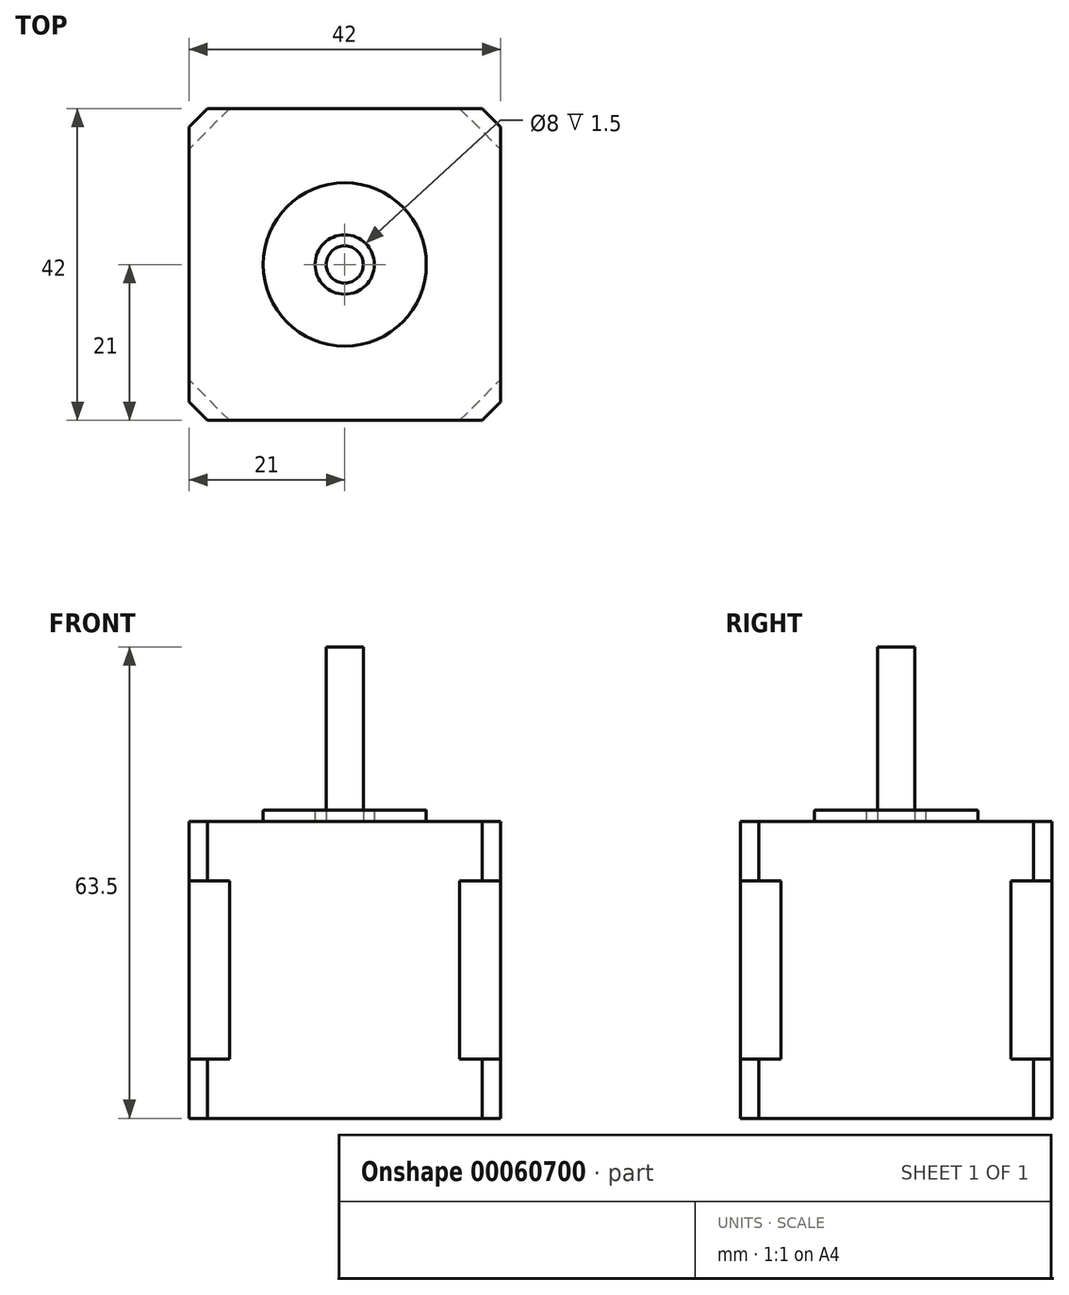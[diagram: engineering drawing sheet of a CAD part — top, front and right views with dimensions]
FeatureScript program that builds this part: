
annotation { "Feature Type Name" : "Feature", "Feature Type Description" : "" }
export const myFeature = defineFeature(function(context is Context, id is Id, definition is map)
    precondition{}
    {
        {
            var Q0;
            Q0=qCreatedBy(makeId("Top.planeOp"),FACE);
            var sketch = newSketch(context, id + "F0", { "sketchPlane" : qUnion([Q0])});
            skLineSegment(sketch, "E0.rect.bottom", {"start": v(21, 21) * mm, "end": v(-21, 21) * mm});
            skLineSegment(sketch, "E0.rect.top", {"start": v(21, -21) * mm, "end": v(-21, -21) * mm});
            skLineSegment(sketch, "E0.rect.left", {"start": v(21, 21) * mm, "end": v(21, -21) * mm});
            skLineSegment(sketch, "E0.rect.right", {"start": v(-21, 21) * mm, "end": v(-21, -21) * mm});
            skPoint(sketch, "E0.rect.middle", {"position": v(0, 0) * mm});
            skSolve(sketch);
        }
        {
            var Q0;
            Q0=makeQuery(id+"F0.imprint","IMPRINT",FACE,{"disambiguationData":[TD([[makeQuery(id+"F0.imprint","IMPRINT",EDGE,{"derivedFrom":sQuery(id+"F0.wireOp",EDGE,"E0.rect.bottom")}),1.0]])]});
            var Q1;
            Q1 = qSketchRegion(id + "FU1vRKXK89ZEF6C_1", true);
            extrude(context, id + "F1", {"entities" : qUnion([Q0, Q1]), "depth" : 8 * mm});
        }
        {
            var Q0;
            Q0=makeQuery(id+"F1.opExtrude","CAP_FACE",FACE,{"disambiguationData":[OSD([sQuery(id+"F0.wireOp",EDGE,"E0.rect.bottom"),sQuery(id+"F0.wireOp",EDGE,"E0.rect.top"),sQuery(id+"F0.wireOp",EDGE,"E0.rect.left"),sQuery(id+"F0.wireOp",EDGE,"E0.rect.right")])],"isStart":false});
            extrude(context, id + "F2", {"entities" : qUnion([Q0]), "depth" : 24 * mm});
        }
        {
            var Q0;
            Q0=makeQuery(id+"F2.opExtrude","CAP_FACE",FACE,{"disambiguationData":[OSD([sQuery(id+"F0.wireOp",EDGE,"E0.rect.bottom"),sQuery(id+"F0.wireOp",EDGE,"E0.rect.top"),sQuery(id+"F0.wireOp",EDGE,"E0.rect.left"),sQuery(id+"F0.wireOp",EDGE,"E0.rect.right")])],"isStart":false});
            extrude(context, id + "F3", {"entities" : qUnion([Q0]), "depth" : 8 * mm});
        }
        {
            var Q0;
            Q0=makeQuery(id+"F1.opExtrude","SWEPT_EDGE",EDGE,{"disambiguationData":[OSD([sQuery(id+"F0.wireOp",EDGE,"E0.rect.top"),sQuery(id+"F0.wireOp",EDGE,"E0.rect.right")])]});
            var Q1;
            Q1=makeQuery(id+"F3.opExtrude","SWEPT_EDGE",EDGE,{"disambiguationData":[OSD([sQuery(id+"F0.wireOp",EDGE,"E0.rect.top"),sQuery(id+"F0.wireOp",EDGE,"E0.rect.right")])]});
            var Q2;
            Q2=makeQuery(id+"F3.opExtrude","SWEPT_EDGE",EDGE,{"disambiguationData":[OSD([sQuery(id+"F0.wireOp",EDGE,"E0.rect.bottom"),sQuery(id+"F0.wireOp",EDGE,"E0.rect.right")])]});
            var Q3;
            Q3=makeQuery(id+"F1.opExtrude","SWEPT_EDGE",EDGE,{"disambiguationData":[OSD([sQuery(id+"F0.wireOp",EDGE,"E0.rect.bottom"),sQuery(id+"F0.wireOp",EDGE,"E0.rect.right")])]});
            var Q4;
            Q4=makeQuery(id+"F3.opExtrude","SWEPT_EDGE",EDGE,{"disambiguationData":[OSD([sQuery(id+"F0.wireOp",EDGE,"E0.rect.bottom"),sQuery(id+"F0.wireOp",EDGE,"E0.rect.left")])]});
            var Q5;
            Q5=makeQuery(id+"F1.opExtrude","SWEPT_EDGE",EDGE,{"disambiguationData":[OSD([sQuery(id+"F0.wireOp",EDGE,"E0.rect.bottom"),sQuery(id+"F0.wireOp",EDGE,"E0.rect.left")])]});
            var Q6;
            Q6=makeQuery(id+"F3.opExtrude","SWEPT_EDGE",EDGE,{"disambiguationData":[OSD([sQuery(id+"F0.wireOp",EDGE,"E0.rect.top"),sQuery(id+"F0.wireOp",EDGE,"E0.rect.left")])]});
            var Q7;
            Q7=makeQuery(id+"F1.opExtrude","SWEPT_EDGE",EDGE,{"disambiguationData":[OSD([sQuery(id+"F0.wireOp",EDGE,"E0.rect.top"),sQuery(id+"F0.wireOp",EDGE,"E0.rect.left")])]});
            chamfer(context, id + "F4", {"entities" : qUnion([Q0, Q1, Q2, Q3, Q4, Q5, Q6, Q7]), "width" : 2.5 * mm, "tangentPropagation" : true});
        }
        {
            var Q0;
            Q0=makeQuery(id+"F2.opExtrude","SWEPT_EDGE",EDGE,{"disambiguationData":[OSD([sQuery(id+"F0.wireOp",EDGE,"E0.rect.top"),sQuery(id+"F0.wireOp",EDGE,"E0.rect.left")])]});
            var Q1;
            Q1=makeQuery(id+"F2.opExtrude","SWEPT_EDGE",EDGE,{"disambiguationData":[OSD([sQuery(id+"F0.wireOp",EDGE,"E0.rect.top"),sQuery(id+"F0.wireOp",EDGE,"E0.rect.right")])]});
            var Q2;
            Q2=makeQuery(id+"F2.opExtrude","SWEPT_EDGE",EDGE,{"disambiguationData":[OSD([sQuery(id+"F0.wireOp",EDGE,"E0.rect.bottom"),sQuery(id+"F0.wireOp",EDGE,"E0.rect.right")])]});
            var Q3;
            Q3=makeQuery(id+"F2.opExtrude","SWEPT_EDGE",EDGE,{"disambiguationData":[OSD([sQuery(id+"F0.wireOp",EDGE,"E0.rect.bottom"),sQuery(id+"F0.wireOp",EDGE,"E0.rect.left")])]});
            chamfer(context, id + "F5", {"entities" : qUnion([Q0, Q1, Q2, Q3]), "width" : 5.5 * mm, "tangentPropagation" : true});
        }
        {
            var Q0;
            Q0=makeQuery(id+"F3.opExtrude","CAP_FACE",FACE,{"disambiguationData":[OSD([sQuery(id+"F0.wireOp",EDGE,"E0.rect.bottom"),sQuery(id+"F0.wireOp",EDGE,"E0.rect.top"),sQuery(id+"F0.wireOp",EDGE,"E0.rect.left"),sQuery(id+"F0.wireOp",EDGE,"E0.rect.right")])],"isStart":false});
            var sketch = newSketch(context, id + "F6", { "sketchPlane" : qUnion([Q0])});
            skCircle(sketch, "E1", {"center": v(0, 0) * mm, "radius": 11 * mm});
            skSolve(sketch);
        }
        {
            var Q0;
            Q0=makeQuery(id+"F6.imprint","IMPRINT",FACE,{"disambiguationData":[TD([[makeQuery(id+"F6.imprint","IMPRINT",EDGE,{"derivedFrom":sQuery(id+"F6.wireOp",EDGE,"E1")}),-1.0]])]});
            var sketch = newSketch(context, id + "F7", { "sketchPlane" : qUnion([Q0])});
            skCircle(sketch, "E2", {"center": v(0, 0) * mm, "radius": 4 * mm});
            skSolve(sketch);
        }
        {
            var Q0;
            Q0=makeQuery(id+"F7.imprint","IMPRINT",FACE,{"disambiguationData":[TD([[makeQuery(id+"F7.imprint","IMPRINT",EDGE,{"derivedFrom":sQuery(id+"F7.wireOp",EDGE,"E2")}),-1.0]])]});
            extrude(context, id + "F8", {"entities" : qUnion([Q0]), "operationType" : NewBodyOperationType.ADD, "depth" : 1.5 * mm});
        }
        {
            var Q0;
            Q0=makeQuery(id+"F6.imprint","IMPRINT",FACE,{"disambiguationData":[TD([[makeQuery(id+"F6.imprint","IMPRINT",EDGE,{"derivedFrom":sQuery(id+"F6.wireOp",EDGE,"E1")}),1.0]])]});
            var sketch = newSketch(context, id + "F9", { "sketchPlane" : qUnion([Q0])});
            skCircle(sketch, "E3", {"center": v(0, 0) * mm, "radius": 2.5 * mm});
            skSolve(sketch);
        }
        {
            var Q0;
            Q0=makeQuery(id+"F9.imprint","IMPRINT",FACE,{"disambiguationData":[TD([[makeQuery(id+"F9.imprint","IMPRINT",EDGE,{"derivedFrom":sQuery(id+"F9.wireOp",EDGE,"E3")}),1.0]])]});
            extrude(context, id + "F10", {"entities" : qUnion([Q0]), "operationType" : NewBodyOperationType.ADD, "depth" : 23.5 * mm});
        }
        {
            var Q0;
            Q0=makeQuery(id+"F1.opExtrude","SWEPT_BODY",BODY,{"disambiguationData":[OSD([sQuery(id+"F0.wireOp",EDGE,"E0.rect.bottom"),sQuery(id+"F0.wireOp",EDGE,"E0.rect.top"),sQuery(id+"F0.wireOp",EDGE,"E0.rect.left"),sQuery(id+"F0.wireOp",EDGE,"E0.rect.right")])]});
            var Q1;
            Q1=makeQuery(id+"F2.opExtrude","SWEPT_BODY",BODY,{"disambiguationData":[OSD([sQuery(id+"F0.wireOp",EDGE,"E0.rect.bottom"),sQuery(id+"F0.wireOp",EDGE,"E0.rect.top"),sQuery(id+"F0.wireOp",EDGE,"E0.rect.left"),sQuery(id+"F0.wireOp",EDGE,"E0.rect.right")])]});
            var Q2;
            Q2=makeQuery(id+"F3.opExtrude","SWEPT_BODY",BODY,{"disambiguationData":[OSD([sQuery(id+"F0.wireOp",EDGE,"E0.rect.bottom"),sQuery(id+"F0.wireOp",EDGE,"E0.rect.top"),sQuery(id+"F0.wireOp",EDGE,"E0.rect.left"),sQuery(id+"F0.wireOp",EDGE,"E0.rect.right")])]});
            booleanBodies(context, id + "F11", {"operationType" : BooleanOperationType.UNION, "tools" : qUnion([Q0, Q1, Q2])});
        }
        {
            var Q0;
            Q0=makeQuery(id+"F8.opExtrude","SWEPT_FACE",FACE,{"disambiguationData":[OSD([sQuery(id+"F6.wireOp",EDGE,"E1")])]});
            fillet(context, id + "F12", {"entities" : qUnion([Q0]), "radius" : 0.1 * mm, "tangentPropagation" : true, "allowEdgeOverflow" : false});
        }
    });
